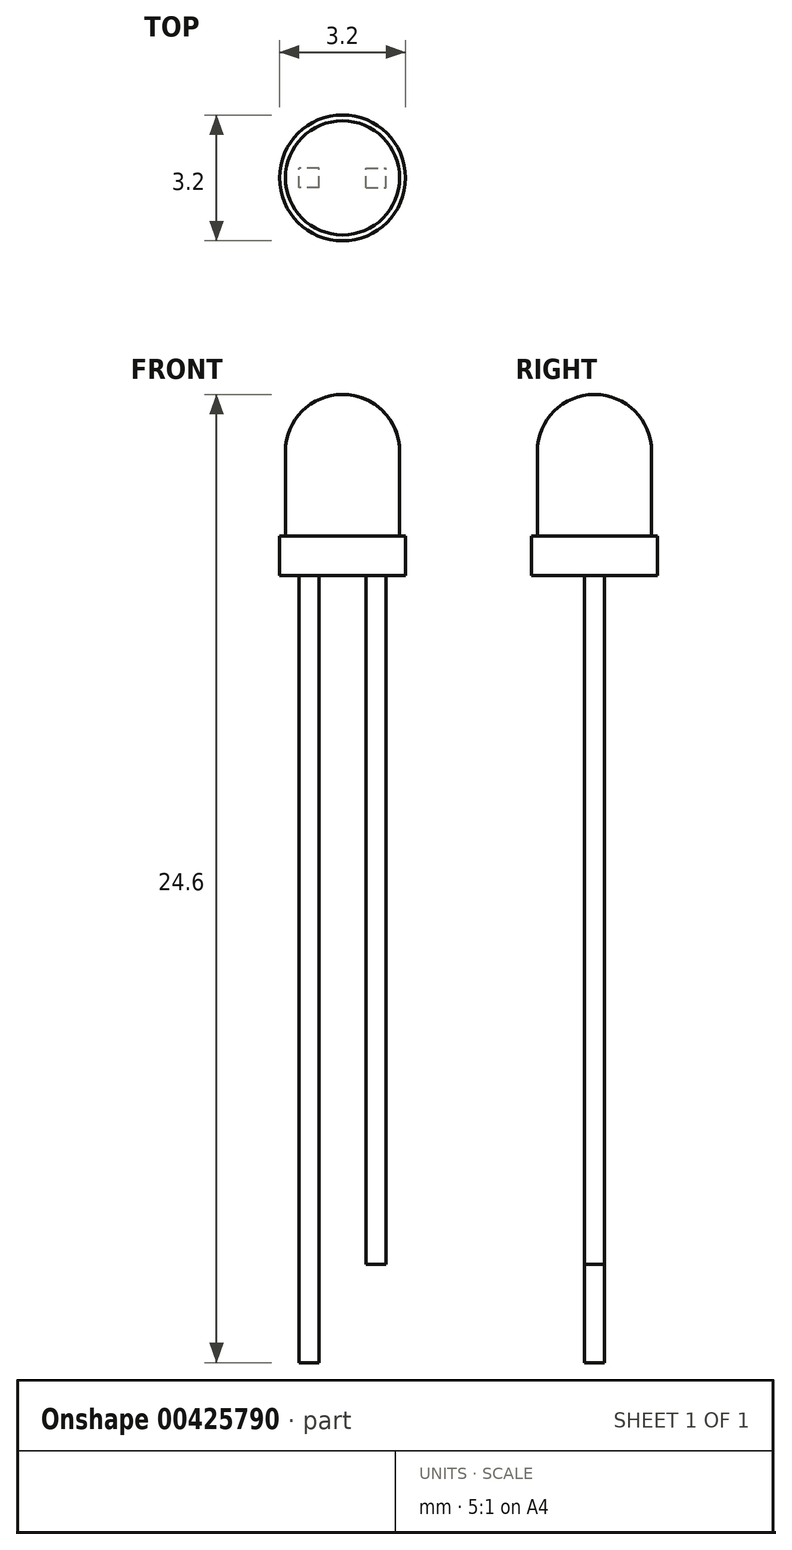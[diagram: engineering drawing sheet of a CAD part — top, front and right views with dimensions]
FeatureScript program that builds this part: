
annotation { "Feature Type Name" : "Feature", "Feature Type Description" : "" }
export const myFeature = defineFeature(function(context is Context, id is Id, definition is map)
    precondition{}
    {
        {
            var Q0;
            Q0=qCreatedBy(makeId("Top.planeOp"),FACE);
            var sketch = newSketch(context, id + "F0", { "sketchPlane" : qUnion([Q0])});
            skCircle(sketch, "E0", {"center": v(0, 0) * mm, "radius": 1.6 * mm});
            skSolve(sketch);
        }
        {
            var Q0;
            Q0 = qSketchRegion(id + "F0", true);
            extrude(context, id + "F1", {"entities" : qUnion([Q0]), "depth" : 1 * mm});
        }
        {
            var Q0;
            Q0=makeQuery(id+"F1.opExtrude","CAP_FACE",FACE,{"disambiguationData":[OSD([sQuery(id+"F0.wireOp",EDGE,"E0")])],"isStart":false});
            var sketch = newSketch(context, id + "F2", { "sketchPlane" : qUnion([Q0])});
            skCircle(sketch, "E1", {"center": v(0, 0) * mm, "radius": 1.45 * mm});
            skSolve(sketch);
        }
        {
            var Q0;
            Q0 = qSketchRegion(id + "F2", true);
            extrude(context, id + "F3", {"entities" : qUnion([Q0]), "operationType" : NewBodyOperationType.ADD, "depth" : 3.6 * mm});
        }
        {
            var Q0;
            Q0=makeQuery(id+"F3.opExtrude","CAP_FACE",FACE,{"disambiguationData":[OSD([sQuery(id+"F2.wireOp",EDGE,"E1")])],"isStart":false});
            fillet(context, id + "F4", {"entities" : qUnion([Q0]), "radius" : 1.45 * mm, "tangentPropagation" : true, "allowEdgeOverflow" : false});
        }
        {
            var Q0;
            Q0=makeQuery(id+"F1.opExtrude","CAP_FACE",FACE,{"disambiguationData":[OSD([sQuery(id+"F0.wireOp",EDGE,"E0")])],"isStart":true});
            var sketch = newSketch(context, id + "F5", { "sketchPlane" : qUnion([Q0])});
            skLineSegment(sketch, "E2.bottom", {"start": v(0.6, 0.25) * mm, "end": v(1.1, 0.25) * mm});
            skLineSegment(sketch, "E2.top", {"start": v(0.6, -0.25) * mm, "end": v(1.1, -0.25) * mm});
            skLineSegment(sketch, "E2.left", {"start": v(0.6, 0.25) * mm, "end": v(0.6, -0.25) * mm});
            skLineSegment(sketch, "E2.right", {"start": v(1.1, 0.25) * mm, "end": v(1.1, -0.25) * mm});
            skLineSegment(sketch, "E3", {"start": v(0, 1.34) * mm, "end": v(0, -1.18) * mm, "construction": true});
            skLineSegment(sketch, "E4.MirrorCS", {"start": v(-0.6, 0.25) * mm, "end": v(-0.6, -0.25) * mm});
            skLineSegment(sketch, "E5.MirrorCS", {"start": v(-0.6, -0.25) * mm, "end": v(-1.1, -0.25) * mm});
            skLineSegment(sketch, "E6.MirrorCS", {"start": v(-1.1, 0.25) * mm, "end": v(-1.1, -0.25) * mm});
            skLineSegment(sketch, "E7.MirrorCS", {"start": v(-0.6, 0.25) * mm, "end": v(-1.1, 0.25) * mm});
            skSolve(sketch);
        }
        {
            var Q0;
            Q0=makeQuery(id+"F5.imprint","IMPRINT",FACE,{"disambiguationData":[TD([[makeQuery(id+"F5.imprint","IMPRINT",EDGE,{"derivedFrom":sQuery(id+"F5.wireOp",EDGE,"E2.bottom")}),-1.0]])]});
            extrude(context, id + "F6", {"entities" : qUnion([Q0]), "depth" : 17.5 * mm});
        }
        {
            var Q0;
            Q0=makeQuery(id+"F5.imprint","IMPRINT",FACE,{"disambiguationData":[TD([[makeQuery(id+"F5.imprint","IMPRINT",EDGE,{"derivedFrom":sQuery(id+"F5.wireOp",EDGE,"E4.MirrorCS")}),-1.0]])]});
            extrude(context, id + "F7", {"entities" : qUnion([Q0]), "depth" : 20 * mm});
        }
    });
